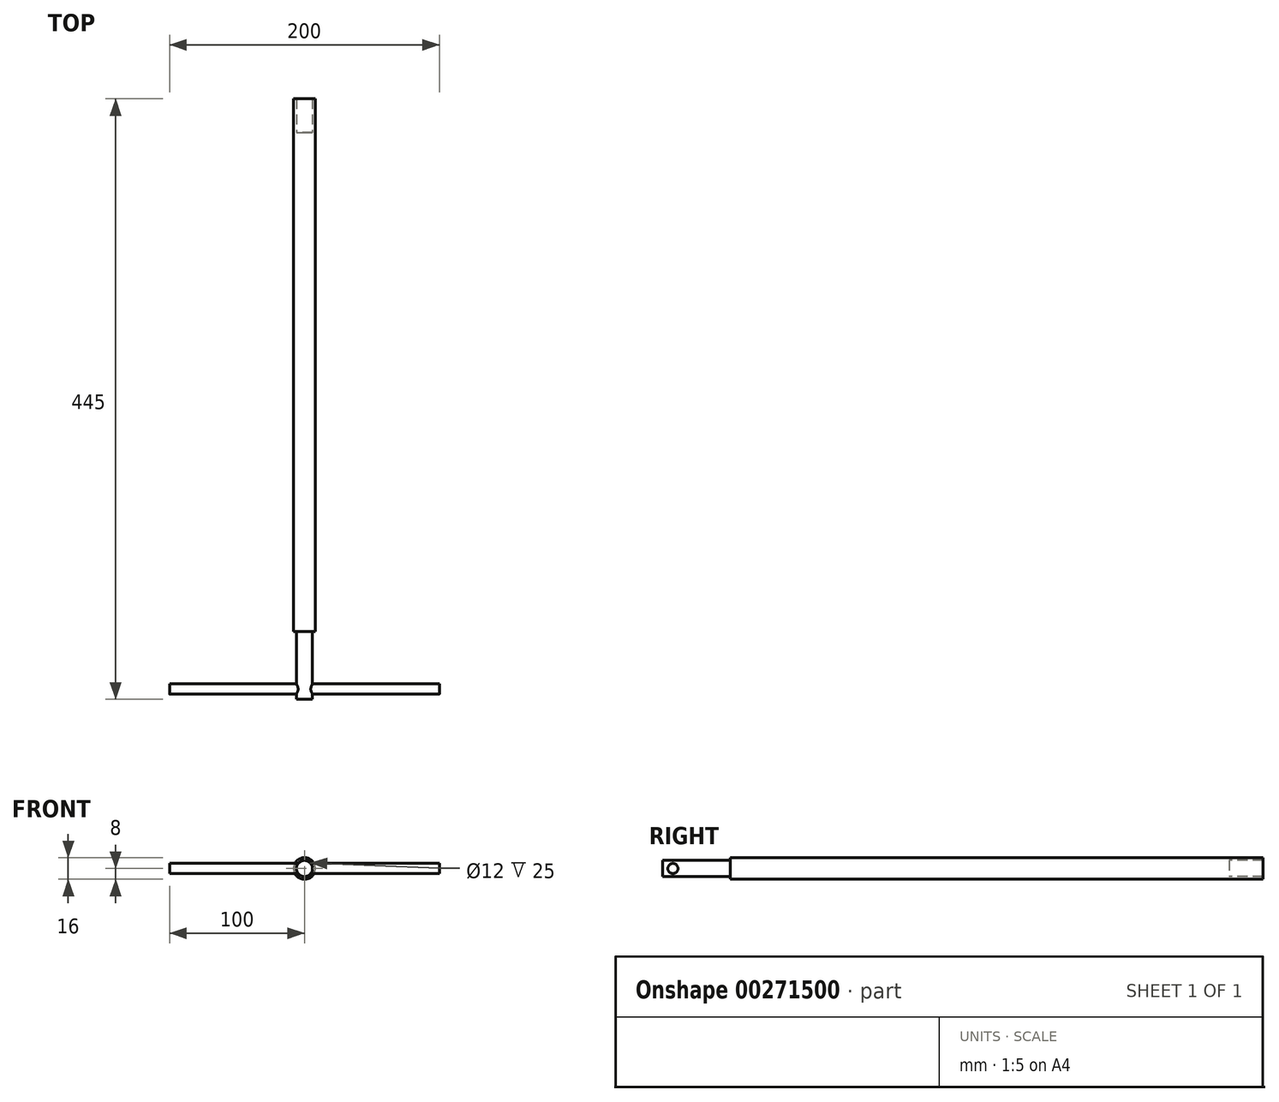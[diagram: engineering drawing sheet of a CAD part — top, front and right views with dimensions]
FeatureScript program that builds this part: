
annotation { "Feature Type Name" : "Feature", "Feature Type Description" : "" }
export const myFeature = defineFeature(function(context is Context, id is Id, definition is map)
    precondition{}
    {
        {
            var Q0;
            Q0=qCreatedBy(makeId("Front.planeOp"),FACE);
            var sketch = newSketch(context, id + "F0", { "sketchPlane" : qUnion([Q0])});
            skCircle(sketch, "E0", {"center": v(0, 0) * mm, "radius": 8 * mm});
            skCircle(sketch, "E1", {"center": v(0, 0) * mm, "radius": 6 * mm});
            skSolve(sketch);
        }
        {
            var Q0;
            Q0 = qSketchRegion(id + "F0", true);
            var Q1;
            Q1=makeQuery(id+"F0.imprint","IMPRINT",FACE,{"disambiguationData":[TD([[makeQuery(id+"F0.imprint","IMPRINT",EDGE,{"derivedFrom":sQuery(id+"F0.wireOp",EDGE,"E1")}),1.0]])]});
            extrude(context, id + "F1", {"entities" : qUnion([Q0, Q1]), "endBound" : BoundingType.SYMMETRIC, "depth" : 370 * mm});
        }
        {
            var Q0;
            Q0=makeQuery(id+"F1.opExtrude","CAP_FACE",FACE,{"disambiguationData":[OSD([sQuery(id+"F0.wireOp",EDGE,"E0")])],"isStart":false});
            var sketch = newSketch(context, id + "F2", { "sketchPlane" : qUnion([Q0])});
            skCircle(sketch, "E2.0", {"center": v(0, 0) * mm, "radius": 6 * mm});
            skSolve(sketch);
        }
        {
            var Q0;
            Q0=makeQuery(id+"F1.opExtrude","CAP_FACE",FACE,{"disambiguationData":[OSD([sQuery(id+"F0.wireOp",EDGE,"E0")])],"isStart":true});
            var sketch = newSketch(context, id + "F3", { "sketchPlane" : qUnion([Q0])});
            skCircle(sketch, "E3.0", {"center": v(0, 0) * mm, "radius": 6 * mm});
            skSolve(sketch);
        }
        {
            var Q0;
            Q0 = qSketchRegion(id + "F2", true);
            extrude(context, id + "F4", {"entities" : qUnion([Q0]), "operationType" : NewBodyOperationType.ADD, "depth" : 50 * mm});
        }
        {
            var Q0;
            Q0=makeQuery(id+"F3.imprint","IMPRINT",FACE,{"disambiguationData":[TD([[makeQuery(id+"F3.imprint","IMPRINT",EDGE,{"derivedFrom":sQuery(id+"F3.wireOp",EDGE,"E3.0")}),-1.0]])]});
            var Q1;
            Q1=sQuery(id+"F3.wireOp",EDGE,"E3.0");
            extrude(context, id + "F5", {"entities" : qUnion([Q0]), "operationType" : NewBodyOperationType.ADD, "surfaceEntities" : qUnion([Q1]), "depth" : 25 * mm});
        }
        {
            var Q0;
            Q0=qCreatedBy(makeId("Right.planeOp"),FACE);
            var sketch = newSketch(context, id + "F6", { "sketchPlane" : qUnion([Q0])});
            skCircle(sketch, "E4", {"center": v(-227.5, 0) * mm, "radius": 3.75 * mm});
            skSolve(sketch);
        }
        {
            var Q0;
            Q0 = qSketchRegion(id + "F6", true);
            extrude(context, id + "F7", {"entities" : qUnion([Q0]), "operationType" : NewBodyOperationType.ADD, "endBound" : BoundingType.SYMMETRIC, "depth" : 200 * mm});
        }
    });
